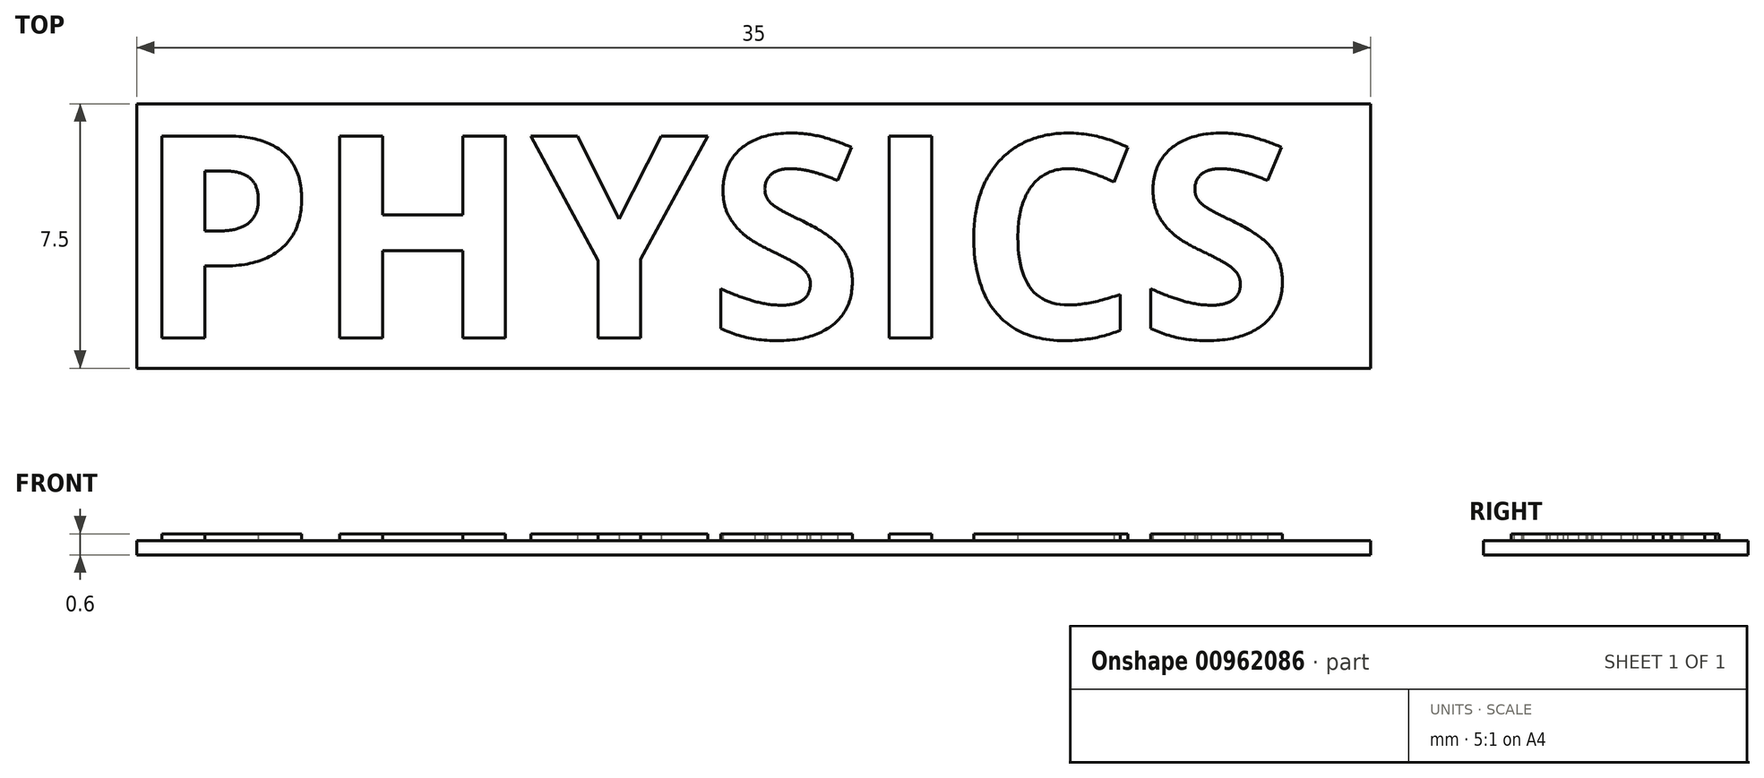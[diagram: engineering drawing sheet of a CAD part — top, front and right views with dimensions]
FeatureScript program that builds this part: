
annotation { "Feature Type Name" : "Feature", "Feature Type Description" : "" }
export const myFeature = defineFeature(function(context is Context, id is Id, definition is map)
    precondition{}
    {
        {
            var Q0;
            Q0=qCreatedBy(makeId("Top.planeOp"),FACE);
            var sketch = newSketch(context, id + "F0", { "sketchPlane" : qUnion([Q0])});
            skLineSegment(sketch, "E0.bottom", {"start": v(17.5, -3.75) * mm, "end": v(-17.5, -3.75) * mm});
            skLineSegment(sketch, "E0.top", {"start": v(17.5, 3.75) * mm, "end": v(-17.5, 3.75) * mm});
            skLineSegment(sketch, "E0.left", {"start": v(17.5, -3.75) * mm, "end": v(17.5, 3.75) * mm});
            skLineSegment(sketch, "E0.right", {"start": v(-17.5, -3.75) * mm, "end": v(-17.5, 3.75) * mm});
            skPoint(sketch, "E0.middle", {"position": v(0, 0) * mm});
            skSolve(sketch);
        }
        {
            var Q0;
            Q0=makeQuery(id+"F0.imprint","IMPRINT",FACE,{"disambiguationData":[TD([[makeQuery(id+"F0.imprint","IMPRINT",EDGE,{"derivedFrom":sQuery(id+"F0.wireOp",EDGE,"E0.bottom")}),-1.0]])]});
            extrude(context, id + "F1", {"entities" : qUnion([Q0]), "depth" : 0.4 * mm, "offsetDistance" : 25 * mm});
        }
        {
            var Q0;
            Q0=makeQuery(id+"F1.opExtrude","CAP_FACE",FACE,{"disambiguationData":[OSD([sQuery(id+"F0.wireOp",EDGE,"E0.bottom"),sQuery(id+"F0.wireOp",EDGE,"E0.top"),sQuery(id+"F0.wireOp",EDGE,"E0.left"),sQuery(id+"F0.wireOp",EDGE,"E0.right")])],"isStart":false});
            var sketch = newSketch(context, id + "F2", { "sketchPlane" : qUnion([Q0])});
            skText(sketch, "E1", { "text": "PHYSICS", "fontName": "OpenSans-Bold.ttf"});
            skPoint(sketch, "E2", {"position": v(-17.5, 0) * mm});
            const initialGuessF2  = {"E1": [-0.0175, -0.00289, 1, 0, 0.00578]};
            skSetInitialGuess(sketch, initialGuessF2);
            skSolve(sketch);
        }
        {
            var Q0;
            Q0 = qSketchRegion(id + "F2", true);
            extrude(context, id + "F3", {"entities" : qUnion([Q0]), "operationType" : NewBodyOperationType.ADD, "depth" : .2 * mm, "offsetDistance" : 25 * mm});
        }
    });
